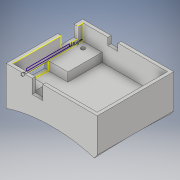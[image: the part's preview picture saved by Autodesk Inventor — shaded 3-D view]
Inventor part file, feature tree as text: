
AUTODESK INVENTOR PART (.ipt)
format: ipt  version: 2017 (Build 210142000, 142)  size: 304,128 bytes
history: native  units: in
note: dims shown in document units (in); Inventor stores cm internally (conversion verified against a paired STEP export)
features: sketch x12, projected_geometry x10, extrude x8, plane x1, mirror x1, hole x1, sweep x1
ambient origin geometry x8: Origin, YZ Plane, XZ Plane, XY Plane, X Axis, Y Axis, Z Axis, Center Point
bodies: Solid1 (feature_tree)
feature tree (34):
  extrude  "Extrusion1"  Depth=2.6732in
  extrude  "Extrusion3"  Depth=0.0984in
  extrude  "Extrusion4"  Depth=0.0984in
  plane  "Work Plane1"
  mirror  "Mirror1"
  extrude  "Extrusion7"  Depth=0.8543in TaperAngle=0.0deg
  hole  "Hole6"  [1 undecoded]
  extrude  "Extrusion8"  Depth=0.4in
  extrude  "Extrusion9"  Depth=0.4291in
  extrude  "Extrusion10"  Depth=1.0787in
  sweep  "Sweep1"
  extrude  "Extrusion11"  Depth=1.0748in
  sketch  "Sketch18"  dims[d97=0.2756in d98=0.0in d99=0.2047in d100=0.2087in d101=0.2047in d102=0.1969in d103=0.1969in d104=0.2087in d105=0.1299in d106=0.2362in d107=0.1575in d108=0.0787in d109=90.0deg d110=0.3543in d111=0.0in d112=0.063in d113=0.7205in d114=0.3386in d116=0.0984in d117=0.0in d118=0.4488in d119=0.6693in d120=0.2362in d122=0.0984in d123=0.0in d124=1.563in d126=0.2756in d127=0.315in d128=0.3937in d129=0.0in d134=0.1575in d136=0.1575in d137=0.0in d138=0.0in d139=0.5118in d140=0.3543in d141=0.2756in d142=0.3937in d143=0.0in d145=0.0669in d147=0.4291in]
  sketch  "Sketch1"  dims[d0=0.0787in d1=0.0in d4=2.6732in]
  sketch  "Sketch4"  dims[d5=2.2165in d35=0.0984in]
  sketch  "Sketch5"  dims[d36=0.0984in d37=0.0984in]
  sketch  "Sketch11"  dims[d38=0.0984in d39=0.8543in d40=0.0in]
  projected_geometry  "Projected Loop3"
  sketch  "Sketch12"  dims[d41=0.2165in d42=1.4in]
  sketch  "Sketch13"  dims[d43=0.0in d44=0.0in d70=0.4in d72=0.375in d73=0.6in]
  sketch  "Sketch14"  dims[d89=0.6063in d90=0.4291in]
  projected_geometry  "Projected Loop4"
  projected_geometry  "Projected Loop5"
  sketch  "Sketch15"  dims[d91=0.6102in d92=1.0787in]
  projected_geometry  "Projected Loop6"
  projected_geometry  "Projected Loop7"
  projected_geometry  "Projected Loop8"
  projected_geometry  "Projected Loop9"
  sketch  "Sketch16"  dims[d93=0.6378in d94=0.4882in]
  sketch  "3D Sketch1"
  projected_geometry  "Projected Loop10"
  sketch  "Sketch17"  dims[d95=0.1575in d96=1.0748in]
  projected_geometry  "Projected Loop11"
  projected_geometry  "Projected Loop12"
note: 1 required parameter value undecoded (feature->parameter linkage not recoverable at this tier; creation-order binding heuristic only, values carry confidence <= 0.55)
